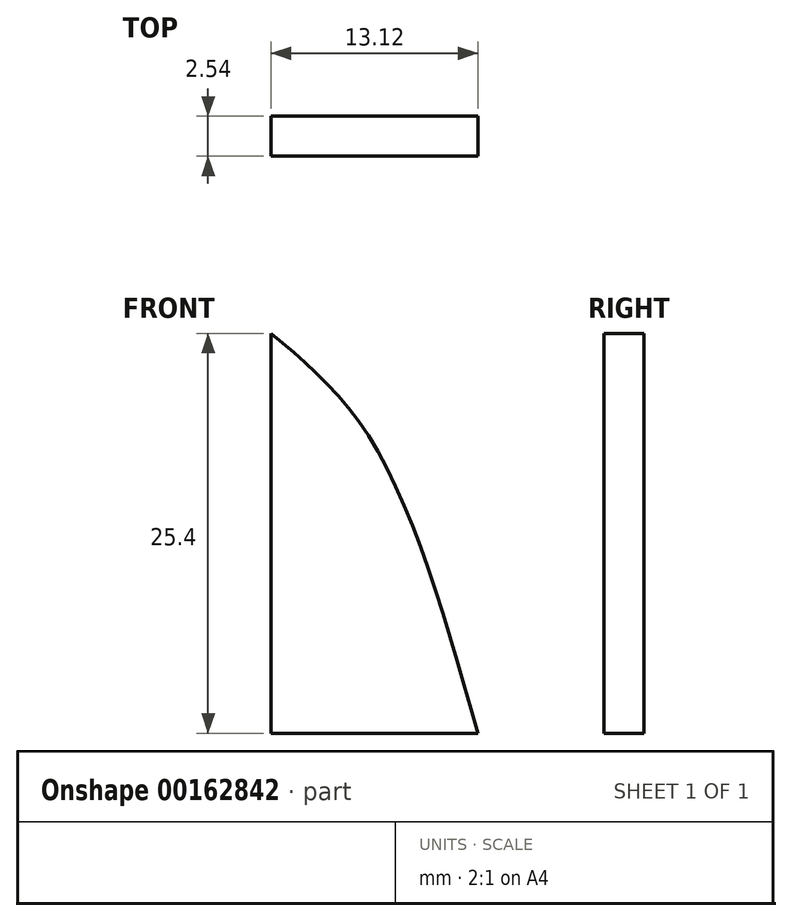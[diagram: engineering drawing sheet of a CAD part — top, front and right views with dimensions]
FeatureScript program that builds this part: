
annotation { "Feature Type Name" : "Feature", "Feature Type Description" : "" }
export const myFeature = defineFeature(function(context is Context, id is Id, definition is map)
    precondition{}
    {
        {
            var Q0;
            Q0=qCreatedBy(makeId("Front.planeOp"),FACE);
            var sketch = newSketch(context, id + "F0", { "sketchPlane" : qUnion([Q0])});
            skLineSegment(sketch, "E0", {"start": v(0, 0) * mm, "end": v(0, 25.4) * mm});
            skFitSpline(sketch, "E1", {"points": [v(0, 25.4) * mm, v(6.41, 18.5) * mm, v(13.12, 0) * mm], "startDerivative": vector(16.57, -13.9) * mm, "endDerivative": vector(10.06, -35.58) * mm});
            skLineSegment(sketch, "E2", {"start": v(13.12, 0) * mm, "end": v(0, 0) * mm});
            skSolve(sketch);
        }
        {
            var Q0;
            Q0=makeQuery(id+"F0.imprint","IMPRINT",FACE,{"disambiguationData":[TD([[makeQuery(id+"F0.imprint","IMPRINT",EDGE,{"derivedFrom":sQuery(id+"F0.wireOp",EDGE,"E0")}),-1.0]])]});
            extrude(context, id + "F1", {"entities" : qUnion([Q0]), "depth" : 2.54 * mm});
        }
    });
